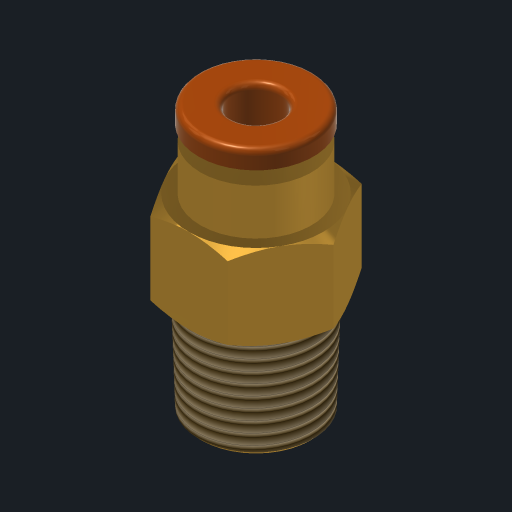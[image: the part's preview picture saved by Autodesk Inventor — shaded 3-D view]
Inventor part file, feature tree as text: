
AUTODESK INVENTOR PART (.ipt)
format: ipt  version: 2023 (Build 270158030, 158C)  size: 252,928 bytes
history: native  units: in
note: dims shown in document units (in); Inventor stores cm internally (conversion verified against a paired STEP export)
features: other x1, imported_body x1, thread x1
ambient origin geometry x8: Origin, YZ Plane, XZ Plane, XY Plane, X Axis, Y Axis, Z Axis, Center Point
bodies: Body1 (feature_tree)
feature tree (3):
  other  "Port"
  imported_body  "Base1"
  thread  "Thread1"  [1 undecoded]
note: 1 required parameter value undecoded (feature->parameter linkage not recoverable at this tier; creation-order binding heuristic only, values carry confidence <= 0.55)
